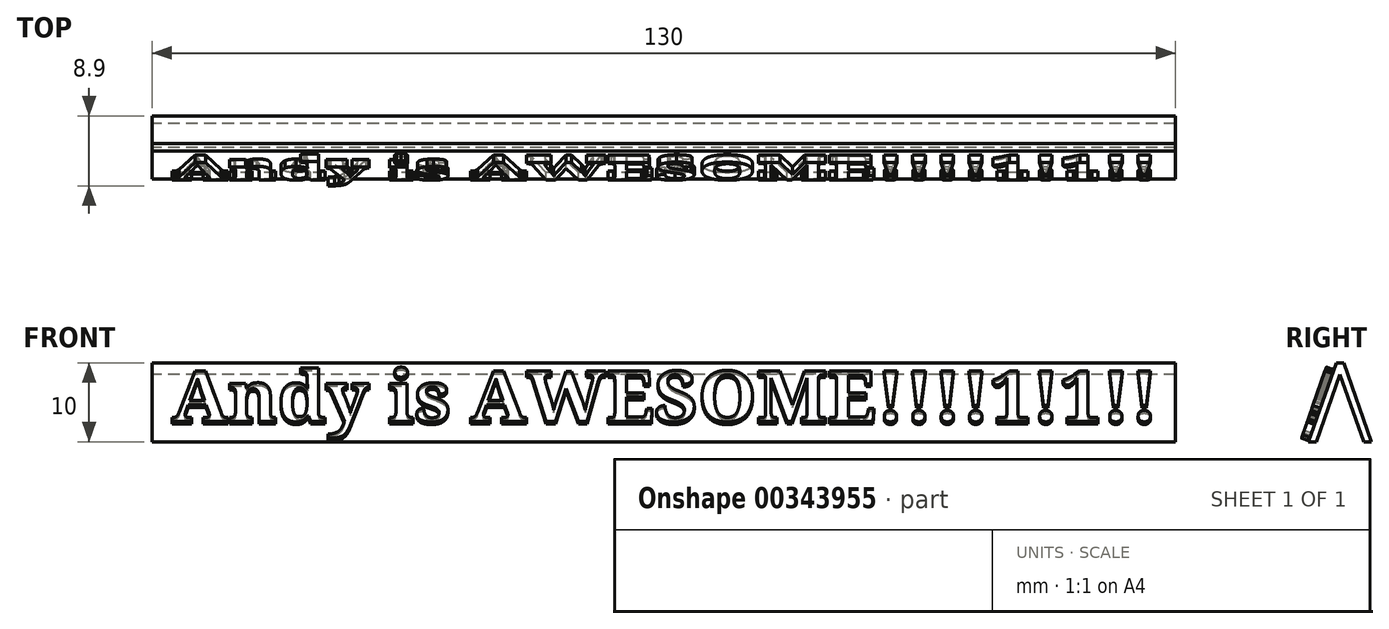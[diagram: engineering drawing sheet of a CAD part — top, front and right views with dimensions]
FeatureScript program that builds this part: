
annotation { "Feature Type Name" : "Feature", "Feature Type Description" : "" }
export const myFeature = defineFeature(function(context is Context, id is Id, definition is map)
    precondition{}
    {
        {
            var Q0;
            Q0=qCreatedBy(makeId("Right.planeOp"),FACE);
            var sketch = newSketch(context, id + "F0", { "sketchPlane" : qUnion([Q0])});
            skLineSegment(sketch, "E0", {"start": v(0, 0) * mm, "end": v(0, 10) * mm, "construction": true});
            skLineSegment(sketch, "E1", {"start": v(0, 0) * mm, "end": v(-3, 0) * mm, "construction": true});
            skLineSegment(sketch, "E2", {"start": v(-3, 0) * mm, "end": v(-4, 0) * mm});
            skLineSegment(sketch, "E3", {"start": v(0, 10) * mm, "end": v(-0.5, 10) * mm});
            skLineSegment(sketch, "E4", {"start": v(-0.5, 10) * mm, "end": v(-4, 0) * mm});
            skLineSegment(sketch, "E5", {"start": v(-3, 0) * mm, "end": v(0, 8.57) * mm});
            skLineSegment(sketch, "E6.MirrorCS", {"start": v(3, 0) * mm, "end": v(0, 8.57) * mm});
            skLineSegment(sketch, "E7.MirrorCS", {"start": v(0.5, 10) * mm, "end": v(4, 0) * mm});
            skLineSegment(sketch, "E8.MirrorCS", {"start": v(0, 10) * mm, "end": v(0.5, 10) * mm});
            skLineSegment(sketch, "E9.MirrorCS", {"start": v(3, 0) * mm, "end": v(4, 0) * mm});
            skSolve(sketch);
        }
        {
            var Q0;
            Q0=makeQuery(id+"F0.imprint","IMPRINT",FACE,{"disambiguationData":[TD([[makeQuery(id+"F0.imprint","IMPRINT",EDGE,{"derivedFrom":sQuery(id+"F0.wireOp",EDGE,"E2")}),-1.0]])]});
            extrude(context, id + "F1", {"entities" : qUnion([Q0]), "endBound" : BoundingType.SYMMETRIC, "depth" : 130 * mm});
        }
        {
            var Q0;
            Q0=makeQuery(id+"F1.opExtrude","SWEPT_FACE",FACE,{"disambiguationData":[OSD([sQuery(id+"F0.wireOp",EDGE,"E4")])]});
            var sketch = newSketch(context, id + "F2", { "sketchPlane" : qUnion([Q0])});
            skLineSegment(sketch, "E10", {"start": v(-65, -1.32) * mm, "end": v(-65, -0.32) * mm, "construction": true});
            skLineSegment(sketch, "E11", {"start": v(-65, -0.32) * mm, "end": v(-64, -0.32) * mm, "construction": true});
            skLineSegment(sketch, "E12", {"start": v(65, -1.32) * mm, "end": v(65, -0.32) * mm, "construction": true});
            skLineSegment(sketch, "E13", {"start": v(65, -0.32) * mm, "end": v(64, -0.32) * mm, "construction": true});
            skLineSegment(sketch, "E14", {"start": v(0, -1.32) * mm, "end": v(0, 1.08) * mm, "construction": true});
            skPoint(sketch, "E14.endSnap0", {"position": v(0, -1.32) * mm});
            skText(sketch, "E15", { "text": "Andy is AWESOME!!!!1!1!!", "fontName": "NotoSerif-Bold.ttf"});
            const initialGuessF2  = {"E15": [-0.0625, 0.00108, 1, 0, 0.00681]};
            skSetInitialGuess(sketch, initialGuessF2);
            skSolve(sketch);
        }
        {
            var Q0;
            Q0 = qSketchRegion(id + "F2", true);
            extrude(context, id + "F3", {"entities" : qUnion([Q0]), "operationType" : NewBodyOperationType.ADD, "depth" : 1 * mm});
        }
    });
